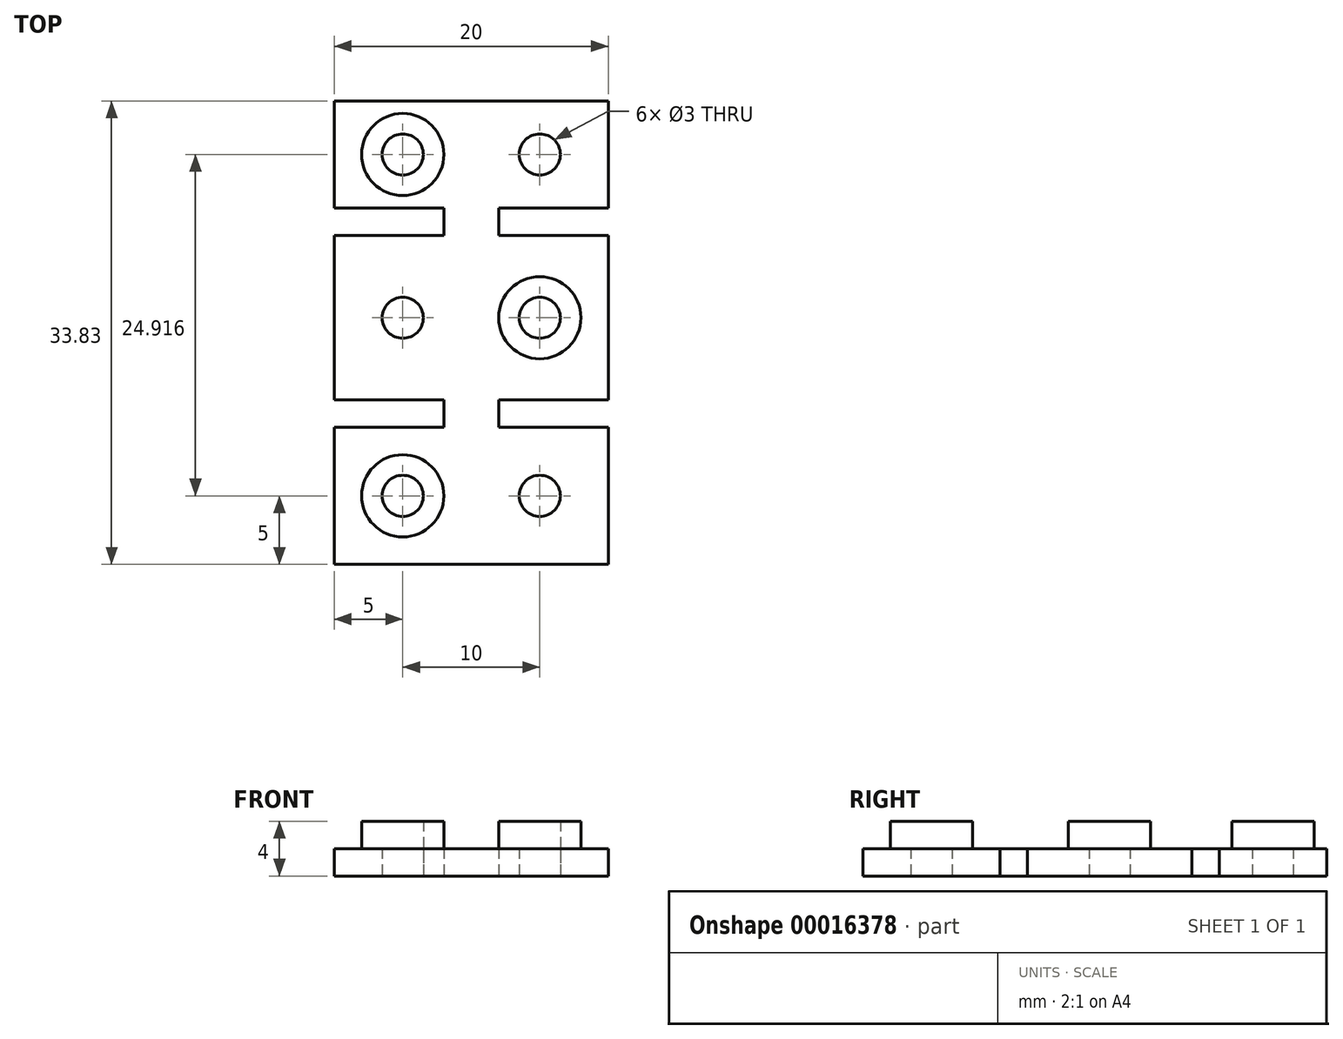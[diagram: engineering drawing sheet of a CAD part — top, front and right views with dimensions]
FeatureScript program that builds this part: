
annotation { "Feature Type Name" : "Feature", "Feature Type Description" : "" }
export const myFeature = defineFeature(function(context is Context, id is Id, definition is map)
    precondition{}
    {
        {
            var Q0;
            Q0=qCreatedBy(makeId("Top.planeOp"),FACE);
            var sketch = newSketch(context, id + "F0", { "sketchPlane" : qUnion([Q0])});
            skLineSegment(sketch, "E0.bottom", {"start": v(-10, 33.83) * mm, "end": v(10, 33.83) * mm});
            skLineSegment(sketch, "E0.top", {"start": v(-10, 0) * mm, "end": v(10, 0) * mm});
            skLineSegment(sketch, "E0.left", {"start": v(-10, 33.83) * mm, "end": v(-10, 26) * mm});
            skLineSegment(sketch, "E0.right", {"start": v(10, 33.83) * mm, "end": v(10, 26) * mm});
            skLineSegment(sketch, "E1", {"start": v(-10, 26) * mm, "end": v(-2, 26) * mm});
            skLineSegment(sketch, "E2", {"start": v(-2, 26) * mm, "end": v(-2, 24) * mm});
            skLineSegment(sketch, "E3", {"start": v(-2, 24) * mm, "end": v(-10, 24) * mm});
            skLineSegment(sketch, "E4", {"start": v(10, 26) * mm, "end": v(2, 26) * mm});
            skLineSegment(sketch, "E5", {"start": v(2, 26) * mm, "end": v(2, 24) * mm});
            skLineSegment(sketch, "E6", {"start": v(2, 24) * mm, "end": v(10, 24) * mm});
            skLineSegment(sketch, "E7", {"start": v(-10, 12) * mm, "end": v(-2, 12) * mm});
            skLineSegment(sketch, "E8", {"start": v(-2, 12) * mm, "end": v(-2, 10) * mm});
            skLineSegment(sketch, "E9", {"start": v(-2, 10) * mm, "end": v(-10, 10) * mm});
            skLineSegment(sketch, "E10", {"start": v(10, 12) * mm, "end": v(2, 12) * mm});
            skLineSegment(sketch, "E11", {"start": v(2, 12) * mm, "end": v(2, 10) * mm});
            skLineSegment(sketch, "E12", {"start": v(2, 10) * mm, "end": v(10, 10) * mm});
            skLineSegment(sketch, "E13.trimOffspring", {"start": v(10, 24) * mm, "end": v(10, 12) * mm});
            skLineSegment(sketch, "E14.trimOffspring", {"start": v(-10, 24) * mm, "end": v(-10, 12) * mm});
            skLineSegment(sketch, "E15.trimOffspring", {"start": v(-10, 10) * mm, "end": v(-10, 0) * mm});
            skLineSegment(sketch, "E16.trimOffspring", {"start": v(10, 10) * mm, "end": v(10, 0) * mm});
            skCircle(sketch, "E17", {"center": v(5, 29.92) * mm, "radius": 1.5 * mm});
            skCircle(sketch, "E18", {"center": v(5, 18) * mm, "radius": 1.5 * mm});
            skCircle(sketch, "E19", {"center": v(5, 5) * mm, "radius": 1.5 * mm});
            skLineSegment(sketch, "E20", {"start": v(5, 33.83) * mm, "end": v(5, 26) * mm, "construction": true});
            skLineSegment(sketch, "E21", {"start": v(5, 24) * mm, "end": v(5, 12) * mm, "construction": true});
            skLineSegment(sketch, "E22", {"start": v(5, 10) * mm, "end": v(5, 0) * mm, "construction": true});
            skCircle(sketch, "E23.MirrorC", {"center": v(-5, 29.92) * mm, "radius": 1.5 * mm});
            skCircle(sketch, "E24.MirrorC", {"center": v(-5, 18) * mm, "radius": 1.5 * mm});
            skCircle(sketch, "E25.MirrorC", {"center": v(-5, 5) * mm, "radius": 1.5 * mm});
            skSolve(sketch);
        }
        {
            var Q0;
            Q0 = qSketchRegion(id + "F0", true);
            extrude(context, id + "F1", {"entities" : qUnion([Q0]), "depth" : 2 * mm});
        }
        {
            var Q0;
            Q0=makeQuery(id+"F1.opExtrude","CAP_FACE",FACE,{"disambiguationData":[OSD([sQuery(id+"F0.wireOp",EDGE,"E0.bottom"),sQuery(id+"F0.wireOp",EDGE,"E0.top"),sQuery(id+"F0.wireOp",EDGE,"E0.left"),sQuery(id+"F0.wireOp",EDGE,"E0.right"),sQuery(id+"F0.wireOp",EDGE,"E1"),sQuery(id+"F0.wireOp",EDGE,"E2"),sQuery(id+"F0.wireOp",EDGE,"E3"),sQuery(id+"F0.wireOp",EDGE,"E4"),sQuery(id+"F0.wireOp",EDGE,"E5"),sQuery(id+"F0.wireOp",EDGE,"E6"),sQuery(id+"F0.wireOp",EDGE,"E7"),sQuery(id+"F0.wireOp",EDGE,"E8"),sQuery(id+"F0.wireOp",EDGE,"E9"),sQuery(id+"F0.wireOp",EDGE,"E10"),sQuery(id+"F0.wireOp",EDGE,"E11"),sQuery(id+"F0.wireOp",EDGE,"E12"),sQuery(id+"F0.wireOp",EDGE,"E13.trimOffspring"),sQuery(id+"F0.wireOp",EDGE,"E14.trimOffspring"),sQuery(id+"F0.wireOp",EDGE,"E15.trimOffspring"),sQuery(id+"F0.wireOp",EDGE,"E16.trimOffspring"),sQuery(id+"F0.wireOp",EDGE,"E17"),sQuery(id+"F0.wireOp",EDGE,"E18"),sQuery(id+"F0.wireOp",EDGE,"E19"),sQuery(id+"F0.wireOp",EDGE,"E23.MirrorC"),sQuery(id+"F0.wireOp",EDGE,"E24.MirrorC"),sQuery(id+"F0.wireOp",EDGE,"E25.MirrorC")])],"isStart":false});
            var sketch = newSketch(context, id + "F2", { "sketchPlane" : qUnion([Q0])});
            skCircle(sketch, "E26.0", {"center": v(-5, 29.92) * mm, "radius": 3 * mm});
            skCircle(sketch, "E27.0", {"center": v(5, 18) * mm, "radius": 3 * mm});
            skCircle(sketch, "E28.0", {"center": v(-5, 5) * mm, "radius": 3 * mm});
            skCircle(sketch, "E29.0", {"center": v(-5, 29.92) * mm, "radius": 1.5 * mm});
            skCircle(sketch, "E30.1", {"center": v(5, 18) * mm, "radius": 1.5 * mm});
            skCircle(sketch, "E31.2", {"center": v(-5, 5) * mm, "radius": 1.5 * mm});
            skSolve(sketch);
        }
        {
            var Q0;
            Q0 = qSketchRegion(id + "F2", true);
            extrude(context, id + "F3", {"entities" : qUnion([Q0]), "operationType" : NewBodyOperationType.ADD, "depth" : 2 * mm});
        }
    });
